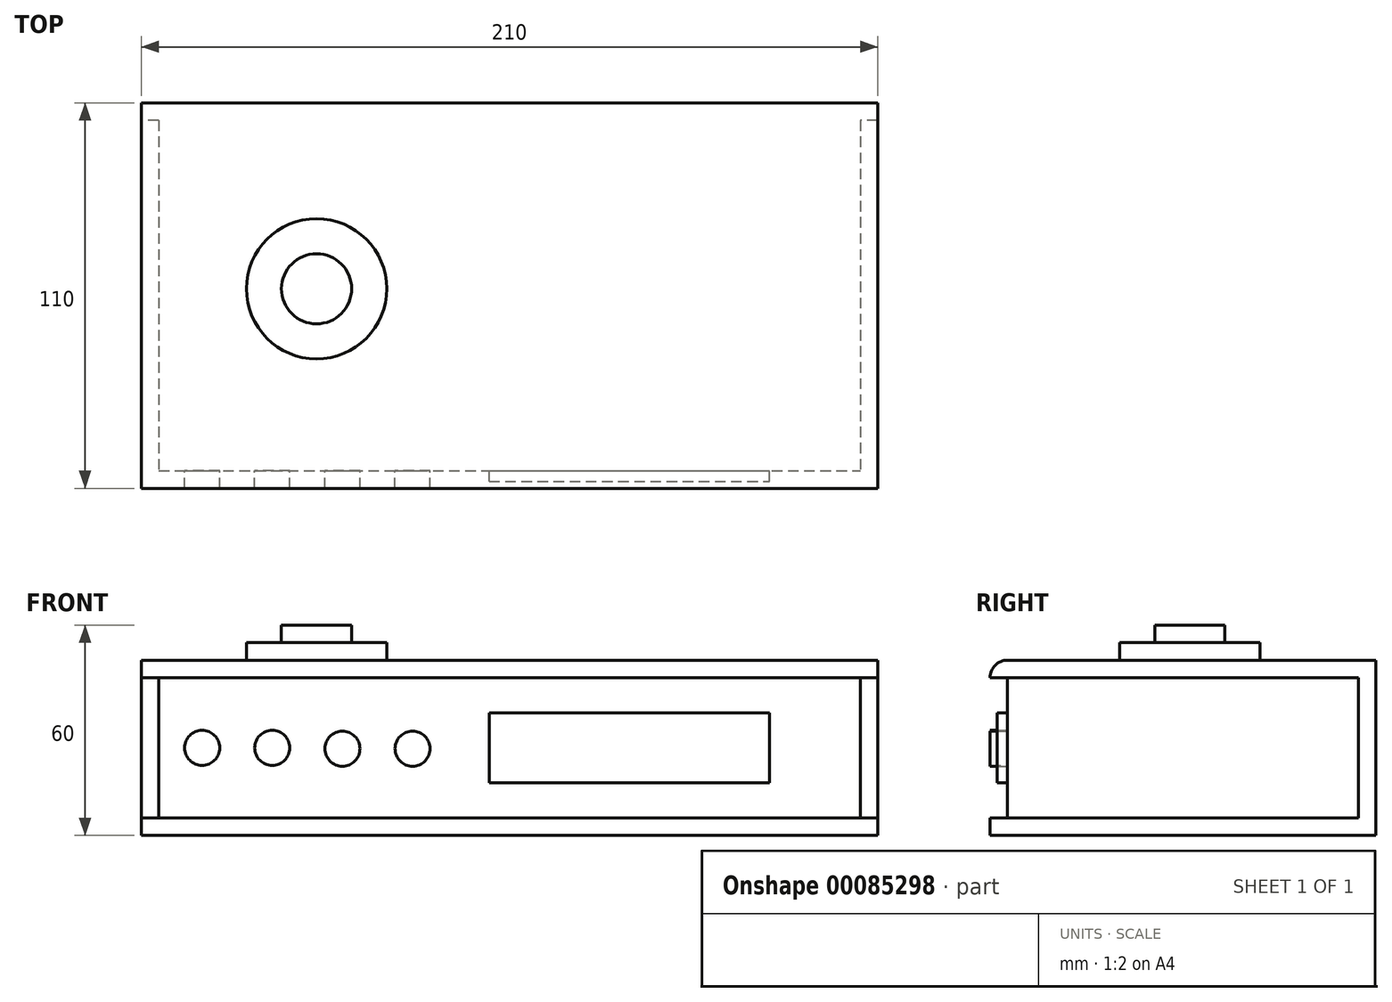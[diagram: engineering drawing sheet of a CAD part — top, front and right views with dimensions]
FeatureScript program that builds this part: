
annotation { "Feature Type Name" : "Feature", "Feature Type Description" : "" }
export const myFeature = defineFeature(function(context is Context, id is Id, definition is map)
    precondition{}
    {
        {
            var Q0;
            Q0=qCreatedBy(makeId("Top.planeOp"),FACE);
            var sketch = newSketch(context, id + "F0", { "sketchPlane" : qUnion([Q0])});
            skLineSegment(sketch, "E0.bottom", {"start": v(-91.05, 48.04) * mm, "end": v(108.95, 48.04) * mm});
            skLineSegment(sketch, "E0.top", {"start": v(-91.05, -51.96) * mm, "end": v(108.95, -51.96) * mm});
            skLineSegment(sketch, "E0.left", {"start": v(-91.05, 48.04) * mm, "end": v(-91.05, -51.96) * mm});
            skLineSegment(sketch, "E0.right", {"start": v(108.95, 48.04) * mm, "end": v(108.95, -51.96) * mm});
            skSolve(sketch);
        }
        {
            var Q0;
            Q0 = qSketchRegion(id + "F0", true);
            extrude(context, id + "F1", {"entities" : qUnion([Q0]), "depth" : 40 * mm});
        }
        {
            var Q0;
            Q0=makeQuery(id+"F1.opExtrude","CAP_FACE",FACE,{"disambiguationData":[OSD([sQuery(id+"F0.wireOp",EDGE,"E0.bottom"),sQuery(id+"F0.wireOp",EDGE,"E0.top"),sQuery(id+"F0.wireOp",EDGE,"E0.left"),sQuery(id+"F0.wireOp",EDGE,"E0.right")])],"isStart":false});
            var sketch = newSketch(context, id + "F2", { "sketchPlane" : qUnion([Q0])});
            skLineSegment(sketch, "E1.bottom", {"start": v(113.95, 48.04) * mm, "end": v(-96.05, 48.04) * mm});
            skLineSegment(sketch, "E1.top", {"start": v(113.95, -56.96) * mm, "end": v(-96.05, -56.96) * mm});
            skLineSegment(sketch, "E1.left", {"start": v(113.95, 48.04) * mm, "end": v(113.95, -56.96) * mm});
            skLineSegment(sketch, "E1.right", {"start": v(-96.05, 48.04) * mm, "end": v(-96.05, -56.96) * mm});
            skSolve(sketch);
        }
        {
            var Q0;
            Q0=makeQuery(id+"F2.imprint","IMPRINT",FACE,{"disambiguationData":[TD([[makeQuery(id+"F2.imprint","IMPRINT",EDGE,{"derivedFrom":sQuery(id+"F2.wireOp",EDGE,"E1.top")}),-1.0]])]});
            var Q1;
            Q1 = qSketchRegion(id + "F2", true);
            var Q2;
            Q2=makeQuery(id+"F2.imprint","IMPRINT",FACE,{"disambiguationData":[TD([[makeQuery(id+"F2.imprint","IMPRINT",EDGE,{"derivedFrom":makeQuery(id+"F1.opExtrude","CAP_EDGE",EDGE,{"disambiguationData":[OSD([sQuery(id+"F0.wireOp",EDGE,"E0.top")])],"isStart":false})}),1.0]])]});
            extrude(context, id + "F3", {"entities" : qUnion([Q0, Q1, Q2]), "operationType" : NewBodyOperationType.ADD, "depth" : 5 * mm});
        }
        {
            var Q0;
            Q0=makeQuery(id+"F1.opExtrude","CAP_FACE",FACE,{"disambiguationData":[OSD([sQuery(id+"F0.wireOp",EDGE,"E0.bottom"),sQuery(id+"F0.wireOp",EDGE,"E0.top"),sQuery(id+"F0.wireOp",EDGE,"E0.left"),sQuery(id+"F0.wireOp",EDGE,"E0.right")])],"isStart":true});
            var sketch = newSketch(context, id + "F4", { "sketchPlane" : qUnion([Q0])});
            skLineSegment(sketch, "E2.bottom", {"start": v(-96.05, -48.04) * mm, "end": v(113.95, -48.04) * mm});
            skLineSegment(sketch, "E2.top", {"start": v(-96.05, 56.96) * mm, "end": v(113.95, 56.96) * mm});
            skLineSegment(sketch, "E2.left", {"start": v(-96.05, -48.04) * mm, "end": v(-96.05, 56.96) * mm});
            skLineSegment(sketch, "E2.right", {"start": v(113.95, -48.04) * mm, "end": v(113.95, 56.96) * mm});
            skSolve(sketch);
        }
        {
            var Q0;
            Q0 = qSketchRegion(id + "F4", true);
            extrude(context, id + "F5", {"entities" : qUnion([Q0]), "operationType" : NewBodyOperationType.ADD, "depth" : 5 * mm});
        }
        {
            var Q0;
            Q0=makeQuery(id+"F5.boolean.opBoolean","MERGE",FACE,{"derivedFrom":[makeQuery(id+"F3.boolean.opBoolean","MERGE",FACE,{"derivedFrom":[makeQuery(id+"F1.opExtrude","SWEPT_FACE",FACE,{"disambiguationData":[OSD([sQuery(id+"F0.wireOp",EDGE,"E0.bottom")])]}),makeQuery(id+"F3.opExtrude","SWEPT_FACE",FACE,{"disambiguationData":[OSD([sQuery(id+"F2.wireOp",EDGE,"E1.bottom")])]})]}),makeQuery(id+"F5.opExtrude","SWEPT_FACE",FACE,{"disambiguationData":[OSD([sQuery(id+"F4.wireOp",EDGE,"E2.bottom")])]})]});
            var sketch = newSketch(context, id + "F6", { "sketchPlane" : qUnion([Q0])});
            skLineSegment(sketch, "E3.bottom", {"start": v(-113.95, 45) * mm, "end": v(96.05, 45) * mm});
            skLineSegment(sketch, "E3.top", {"start": v(-113.95, -5) * mm, "end": v(96.05, -5) * mm});
            skLineSegment(sketch, "E3.left", {"start": v(-113.95, 45) * mm, "end": v(-113.95, -5) * mm});
            skLineSegment(sketch, "E3.right", {"start": v(96.05, 45) * mm, "end": v(96.05, -5) * mm});
            skSolve(sketch);
        }
        {
            var Q0;
            Q0 = qSketchRegion(id + "F6", true);
            extrude(context, id + "F7", {"entities" : qUnion([Q0]), "operationType" : NewBodyOperationType.ADD, "depth" : 5 * mm});
        }
        {
            var Q0;
            Q0=makeQuery(id+"F7.boolean.opBoolean","MERGE",FACE,{"derivedFrom":[makeQuery(id+"F3.opExtrude","CAP_FACE",FACE,{"disambiguationData":[OSD([sQuery(id+"F2.wireOp",EDGE,"E1.bottom"),sQuery(id+"F2.wireOp",EDGE,"E1.top"),sQuery(id+"F2.wireOp",EDGE,"E1.left"),sQuery(id+"F2.wireOp",EDGE,"E1.right")])],"isStart":false}),makeQuery(id+"F7.opExtrude","SWEPT_FACE",FACE,{"disambiguationData":[OSD([sQuery(id+"F6.wireOp",EDGE,"E3.bottom")])]})]});
            var sketch = newSketch(context, id + "F8", { "sketchPlane" : qUnion([Q0])});
            skCircle(sketch, "E4", {"center": v(-46.05, 0) * mm, "radius": 20 * mm});
            skSolve(sketch);
        }
        {
            var Q0;
            Q0=makeQuery(id+"F8.imprint","IMPRINT",FACE,{"disambiguationData":[TD([[makeQuery(id+"F8.imprint","IMPRINT",EDGE,{"derivedFrom":sQuery(id+"F8.wireOp",EDGE,"E4")}),1.0]])]});
            extrude(context, id + "F9", {"entities" : qUnion([Q0]), "operationType" : NewBodyOperationType.ADD, "depth" : 5 * mm});
        }
        {
            var Q0;
            Q0=makeQuery(id+"F9.opExtrude","CAP_FACE",FACE,{"disambiguationData":[OSD([sQuery(id+"F8.wireOp",EDGE,"E4")])],"isStart":false});
            var sketch = newSketch(context, id + "F10", { "sketchPlane" : qUnion([Q0])});
            skCircle(sketch, "E5", {"center": v(-46.05, 0) * mm, "radius": 10 * mm});
            skSolve(sketch);
        }
        {
            var Q0;
            Q0 = qSketchRegion(id + "F10", true);
            extrude(context, id + "F11", {"entities" : qUnion([Q0]), "operationType" : NewBodyOperationType.ADD, "depth" : 5 * mm});
        }
        {
            var Q0;
            Q0=makeQuery(id+"F1.opExtrude","SWEPT_FACE",FACE,{"disambiguationData":[OSD([sQuery(id+"F0.wireOp",EDGE,"E0.top")])]});
            var sketch = newSketch(context, id + "F12", { "sketchPlane" : qUnion([Q0])});
            skCircle(sketch, "E6", {"center": v(-78.68, 20) * mm, "radius": 5 * mm});
            skCircle(sketch, "E7", {"center": v(-58.68, 20) * mm, "radius": 5 * mm});
            skCircle(sketch, "E8", {"center": v(-38.68, 19.76) * mm, "radius": 5 * mm});
            skCircle(sketch, "E9", {"center": v(-18.68, 19.76) * mm, "radius": 5 * mm});
            skLineSegment(sketch, "E10.bottom", {"start": v(3.13, 30) * mm, "end": v(83.13, 30) * mm});
            skLineSegment(sketch, "E10.top", {"start": v(3.13, 10) * mm, "end": v(83.13, 10) * mm});
            skLineSegment(sketch, "E10.left", {"start": v(3.13, 30) * mm, "end": v(3.13, 10) * mm});
            skLineSegment(sketch, "E10.right", {"start": v(83.13, 30) * mm, "end": v(83.13, 10) * mm});
            skSolve(sketch);
        }
        {
            var Q0;
            Q0=makeQuery(id+"F12.imprint","IMPRINT",FACE,{"disambiguationData":[TD([[makeQuery(id+"F12.imprint","IMPRINT",EDGE,{"derivedFrom":sQuery(id+"F12.wireOp",EDGE,"E6")}),1.0]])]});
            extrude(context, id + "F13", {"entities" : qUnion([Q0]), "operationType" : NewBodyOperationType.ADD, "depth" : 5 * mm});
        }
        {
            var Q0;
            Q0=makeQuery(id+"F12.imprint","IMPRINT",FACE,{"disambiguationData":[TD([[makeQuery(id+"F12.imprint","IMPRINT",EDGE,{"derivedFrom":sQuery(id+"F12.wireOp",EDGE,"E7")}),1.0]])]});
            extrude(context, id + "F14", {"entities" : qUnion([Q0]), "operationType" : NewBodyOperationType.ADD, "depth" : 5 * mm});
        }
        {
            var Q0;
            Q0=makeQuery(id+"F12.imprint","IMPRINT",FACE,{"disambiguationData":[TD([[makeQuery(id+"F12.imprint","IMPRINT",EDGE,{"derivedFrom":sQuery(id+"F12.wireOp",EDGE,"E8")}),1.0]])]});
            extrude(context, id + "F15", {"entities" : qUnion([Q0]), "operationType" : NewBodyOperationType.ADD, "depth" : 5 * mm});
        }
        {
            var Q0;
            Q0=makeQuery(id+"F12.imprint","IMPRINT",FACE,{"disambiguationData":[TD([[makeQuery(id+"F12.imprint","IMPRINT",EDGE,{"derivedFrom":sQuery(id+"F12.wireOp",EDGE,"E9")}),1.0]])]});
            extrude(context, id + "F16", {"entities" : qUnion([Q0]), "operationType" : NewBodyOperationType.ADD, "depth" : 5 * mm});
        }
        {
            var Q0;
            Q0=makeQuery(id+"F12.imprint","IMPRINT",FACE,{"disambiguationData":[TD([[makeQuery(id+"F12.imprint","IMPRINT",EDGE,{"derivedFrom":sQuery(id+"F12.wireOp",EDGE,"E10.bottom")}),-1.0]])]});
            extrude(context, id + "F17", {"entities" : qUnion([Q0]), "operationType" : NewBodyOperationType.ADD, "depth" : 3 * mm});
        }
        {
            var Q0;
            Q0=makeQuery(id+"F3.opExtrude","CAP_EDGE",EDGE,{"disambiguationData":[OSD([sQuery(id+"F2.wireOp",EDGE,"E1.top")])],"isStart":false});
            fillet(context, id + "F18", {"entities" : qUnion([Q0]), "radius" : 5 * mm, "tangentPropagation" : true, "allowEdgeOverflow" : false});
        }
    });
